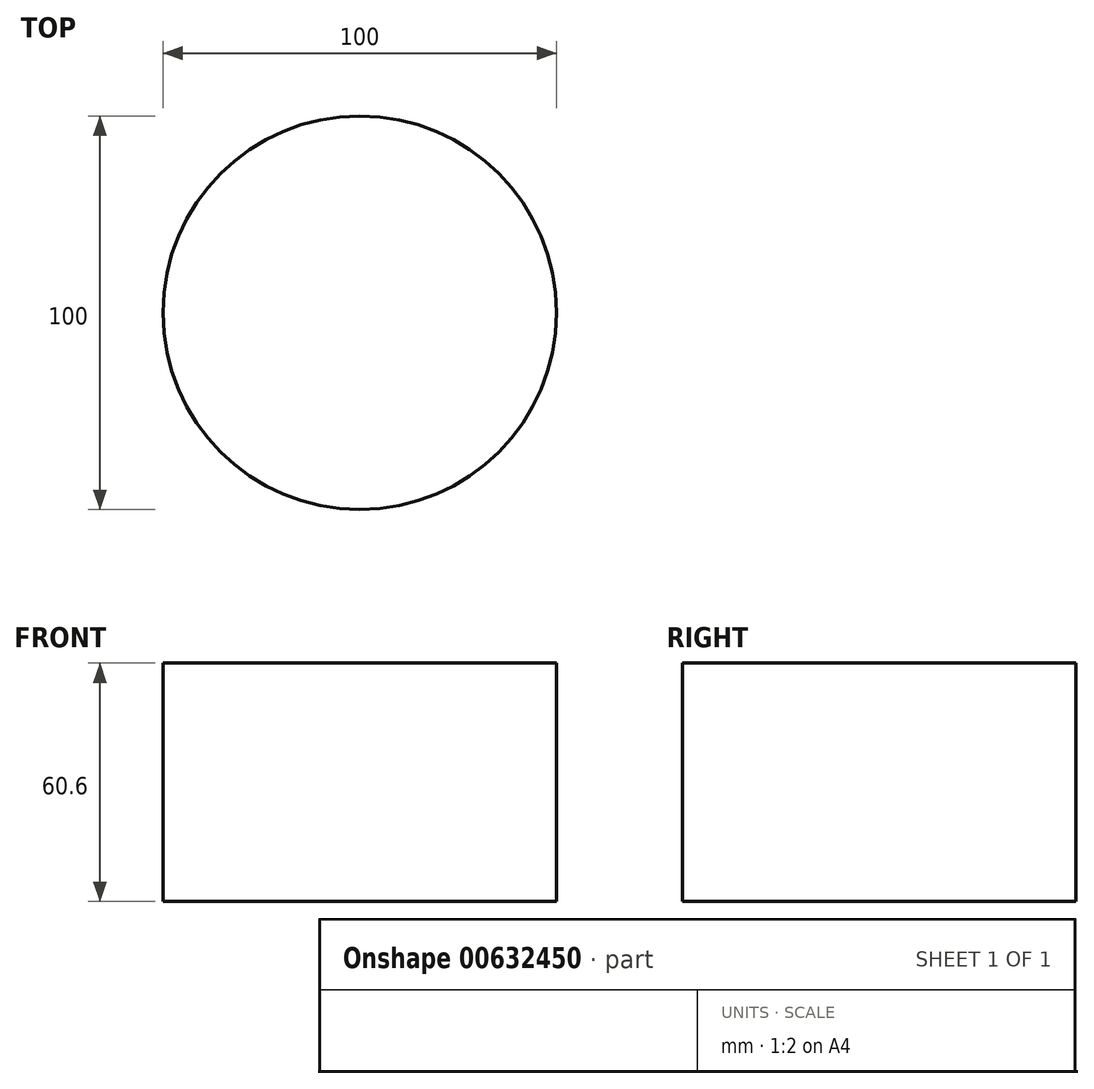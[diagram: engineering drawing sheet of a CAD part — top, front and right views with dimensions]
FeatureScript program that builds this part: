
annotation { "Feature Type Name" : "Feature", "Feature Type Description" : "" }
export const myFeature = defineFeature(function(context is Context, id is Id, definition is map)
    precondition{}
    {
        {
            var Q0;
            Q0=qCreatedBy(makeId("Top.planeOp"),FACE);
            var sketch = newSketch(context, id + "F0", { "sketchPlane" : qUnion([Q0])});
            skCircle(sketch, "E0", {"center": v(-44.27, 27.97) * mm, "radius": 50 * mm});
            skSolve(sketch);
        }
        {
            var Q0;
            Q0=makeQuery(id+"F0.imprint","IMPRINT",FACE,{"disambiguationData":[TD([[makeQuery(id+"F0.imprint","IMPRINT",EDGE,{"derivedFrom":sQuery(id+"F0.wireOp",EDGE,"E0")}),1.0]])]});
            var Q1;
            Q1=sQuery(id+"F0.wireOp",EDGE,"E0");
            extrude(context, id + "F1", {"entities" : qUnion([Q0]), "surfaceEntities" : qUnion([Q1]), "depth" : 60.6 * mm, "offsetDistance" : 25 * mm});
        }
    });
